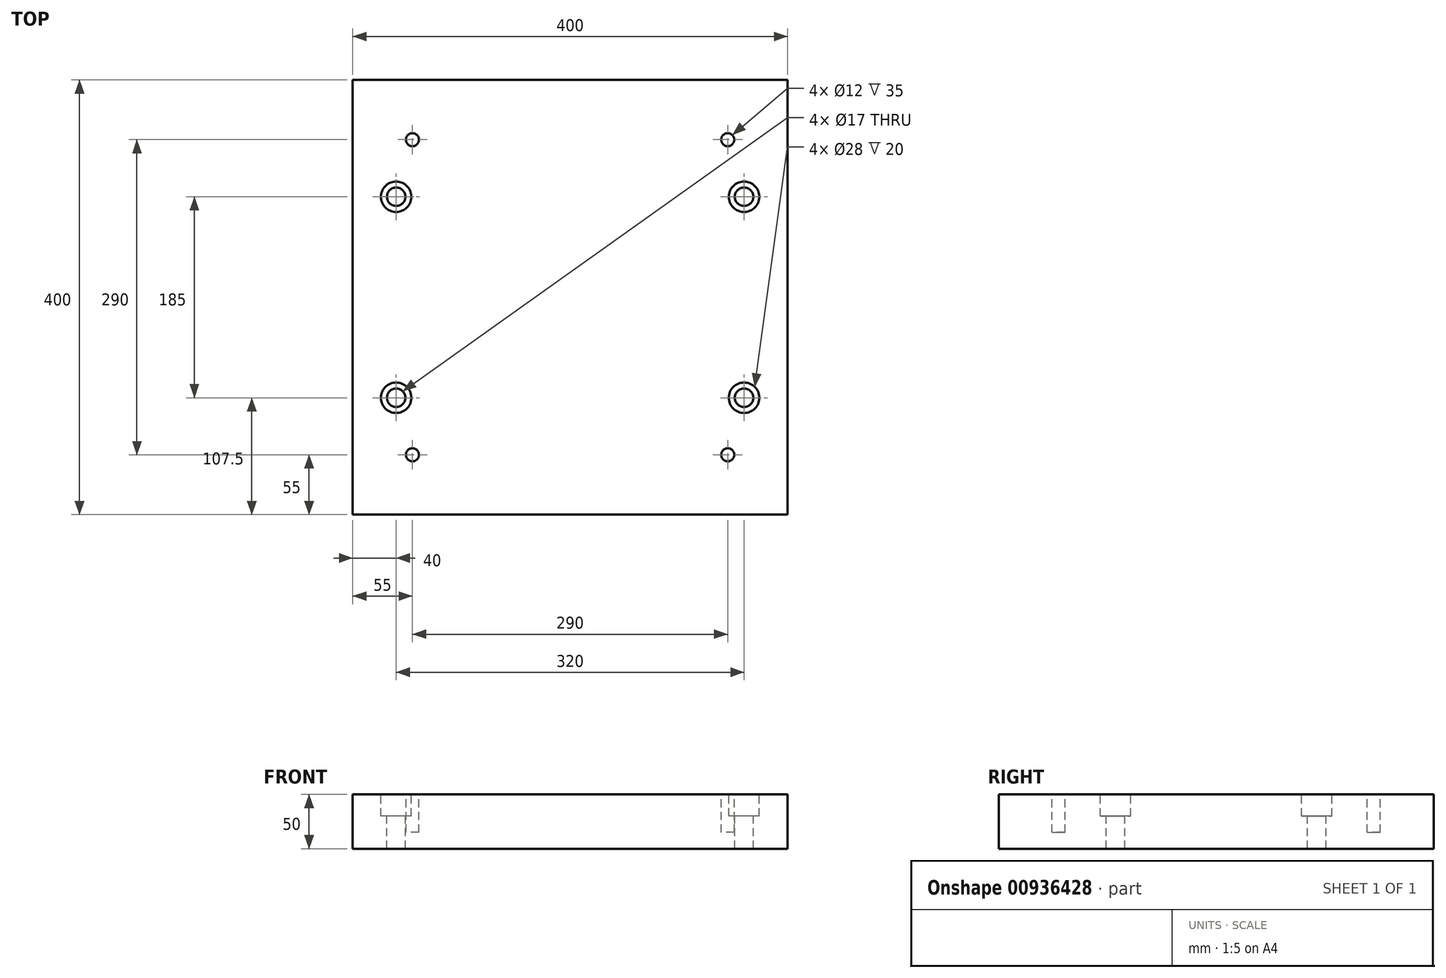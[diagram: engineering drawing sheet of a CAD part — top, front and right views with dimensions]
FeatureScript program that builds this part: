
annotation { "Feature Type Name" : "Feature", "Feature Type Description" : "" }
export const myFeature = defineFeature(function(context is Context, id is Id, definition is map)
    precondition{}
    {
        {
            var Q0;
            Q0=qCreatedBy(makeId("Top.planeOp"),FACE);
            var sketch = newSketch(context, id + "F0", { "sketchPlane" : qUnion([Q0])});
            skLineSegment(sketch, "E0.bottom", {"start": v(200, -200) * mm, "end": v(-200, -200) * mm});
            skLineSegment(sketch, "E0.top", {"start": v(200, 200) * mm, "end": v(-200, 200) * mm});
            skLineSegment(sketch, "E0.left", {"start": v(200, -200) * mm, "end": v(200, 200) * mm});
            skLineSegment(sketch, "E0.right", {"start": v(-200, -200) * mm, "end": v(-200, 200) * mm});
            skPoint(sketch, "E0.middle", {"position": v(0, 0) * mm});
            skSolve(sketch);
        }
        {
            var Q0;
            Q0 = qSketchRegion(id + "F0", true);
            extrude(context, id + "F1", {"entities" : qUnion([Q0]), "oppositeDirection" : true, "depth" : 50 * mm, "offsetDistance" : 25 * mm});
        }
        {
            var Q0;
            Q0=makeQuery(id+"F1.opExtrude","CAP_FACE",FACE,{"disambiguationData":[OSD([sQuery(id+"F0.wireOp",EDGE,"E0.bottom"),sQuery(id+"F0.wireOp",EDGE,"E0.top"),sQuery(id+"F0.wireOp",EDGE,"E0.left"),sQuery(id+"F0.wireOp",EDGE,"E0.right")])],"isStart":true});
            var sketch = newSketch(context, id + "F2", { "sketchPlane" : qUnion([Q0])});
            skCircle(sketch, "E1", {"center": v(145, 145) * mm, "radius": 6 * mm});
            skCircle(sketch, "E2.0.1.0", {"center": v(145, -145) * mm, "radius": 6 * mm});
            skCircle(sketch, "E2.1.0.0", {"center": v(-145, 145) * mm, "radius": 6 * mm});
            skCircle(sketch, "E2.1.1.0", {"center": v(-145, -145) * mm, "radius": 6 * mm});
            skLineSegment(sketch, "E2.direction1", {"start": v(145, 145) * mm, "end": v(-145, 145) * mm, "construction": true});
            skLineSegment(sketch, "E2.direction2", {"start": v(145, 145) * mm, "end": v(145, -145) * mm, "construction": true});
            skSolve(sketch);
        }
        {
            var Q0;
            Q0 = qSketchRegion(id + "F2", true);
            extrude(context, id + "F3", {"entities" : qUnion([Q0]), "operationType" : NewBodyOperationType.REMOVE, "oppositeDirection" : true, "depth" : 35 * mm, "offsetDistance" : 25 * mm});
        }
        {
            var Q0;
            Q0=makeQuery(id+"F1.opExtrude","CAP_FACE",FACE,{"disambiguationData":[OSD([sQuery(id+"F0.wireOp",EDGE,"E0.bottom"),sQuery(id+"F0.wireOp",EDGE,"E0.top"),sQuery(id+"F0.wireOp",EDGE,"E0.left"),sQuery(id+"F0.wireOp",EDGE,"E0.right")])],"isStart":true});
            var sketch = newSketch(context, id + "F4", { "sketchPlane" : qUnion([Q0])});
            skCircle(sketch, "E3", {"center": v(160, 92.5) * mm, "radius": 14 * mm});
            skCircle(sketch, "E4.0.1.0", {"center": v(160, -92.5) * mm, "radius": 14 * mm});
            skCircle(sketch, "E4.1.0.0", {"center": v(-160, 92.5) * mm, "radius": 14 * mm});
            skCircle(sketch, "E4.1.1.0", {"center": v(-160, -92.5) * mm, "radius": 14 * mm});
            skLineSegment(sketch, "E4.direction1", {"start": v(160, 92.5) * mm, "end": v(-160, 92.5) * mm, "construction": true});
            skLineSegment(sketch, "E4.direction2", {"start": v(160, 92.5) * mm, "end": v(160, -92.5) * mm, "construction": true});
            skSolve(sketch);
        }
        {
            var Q0;
            Q0=sQuery(id+"F4.wireOp",VERTEX,"E4.direction1.start");
            var Q1;
            Q1=sQuery(id+"F4.wireOp",VERTEX,"E4.direction2.end");
            var Q2;
            Q2=sQuery(id+"F4.wireOp",VERTEX,"E4.1.1.0.center");
            var Q3;
            Q3=sQuery(id+"F4.wireOp",VERTEX,"E4.direction1.end");
            var Q4;
            Q4=makeQuery(id+"F1.opExtrude","SWEPT_BODY",BODY,{"disambiguationData":[OSD([sQuery(id+"F0.wireOp",EDGE,"E0.bottom"),sQuery(id+"F0.wireOp",EDGE,"E0.top"),sQuery(id+"F0.wireOp",EDGE,"E0.left"),sQuery(id+"F0.wireOp",EDGE,"E0.right")])]});
            hole(context, id + "F5", {"style" : HoleStyle.C_BORE, "endStyle" : HoleEndStyle.BLIND, "holeDiameter" : 17 * mm, "cBoreDiameter" : 28 * mm, "cBoreDepth" : 20 * mm, "majorDiameter" : 5 * mm, "holeDepth" : 53 * mm, "isTappedThrough" : true, "tappedDepth" : 16 * mm, "tapClearance" : 3, "startFromSketch" : true, "locations" : qUnion([Q0, Q1, Q2, Q3]), "scope" : qUnion([Q4])});
        }
    });
